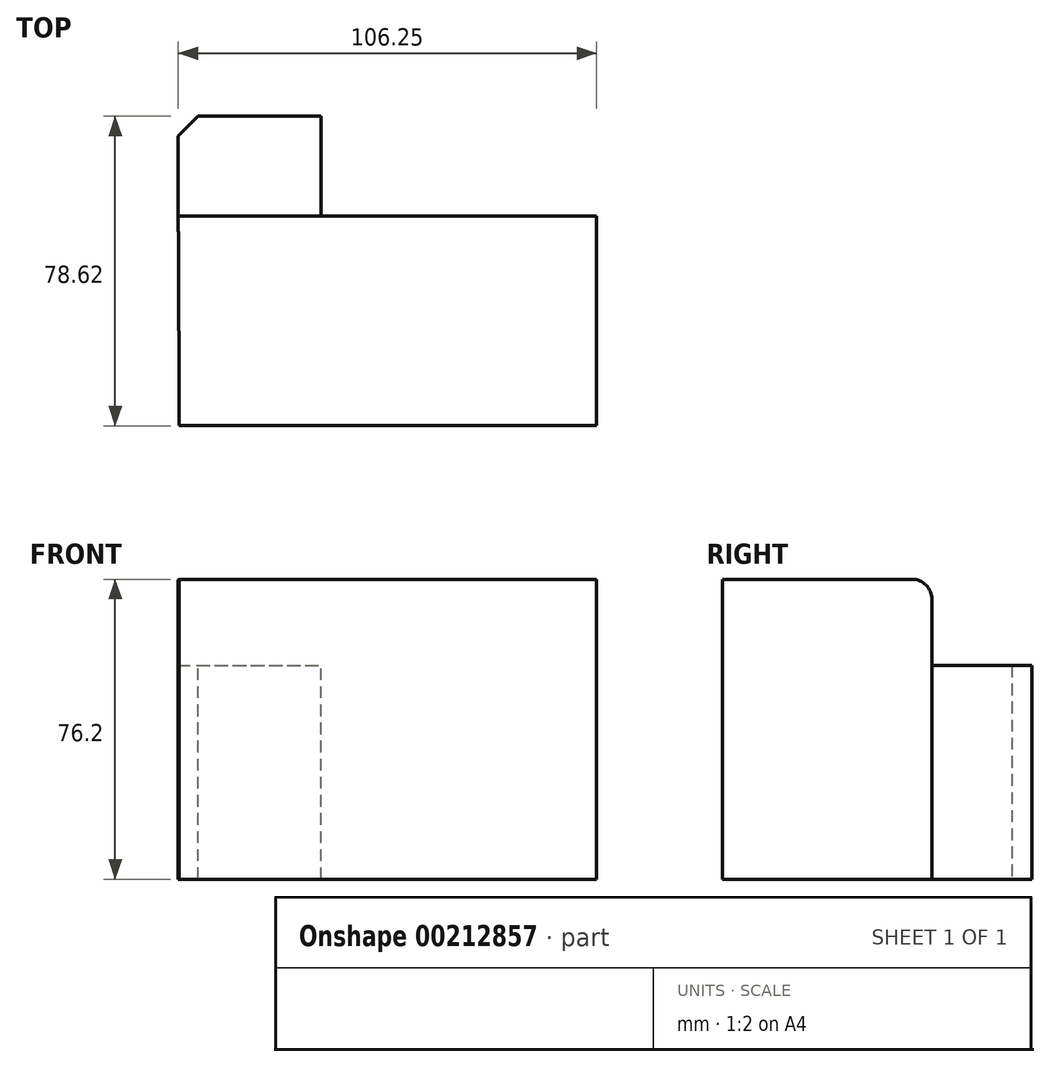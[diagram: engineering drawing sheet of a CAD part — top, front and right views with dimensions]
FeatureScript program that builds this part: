
annotation { "Feature Type Name" : "Feature", "Feature Type Description" : "" }
export const myFeature = defineFeature(function(context is Context, id is Id, definition is map)
    precondition{}
    {
        {
            var Q0;
            Q0=qCreatedBy(makeId("Top.planeOp"),FACE);
            var sketch = newSketch(context, id + "F0", { "sketchPlane" : qUnion([Q0])});
            skLineSegment(sketch, "E0", {"start": v(-76.37, 7.19) * mm, "end": v(29.88, 7.19) * mm});
            skLineSegment(sketch, "E1", {"start": v(29.88, 7.19) * mm, "end": v(29.88, -46.03) * mm});
            skLineSegment(sketch, "E2", {"start": v(29.88, -46.03) * mm, "end": v(-76.18, -46.03) * mm});
            skLineSegment(sketch, "E3", {"start": v(-76.37, 7.19) * mm, "end": v(-76.18, -46.03) * mm});
            skSolve(sketch);
        }
        {
            var Q0;
            Q0 = qSketchRegion(id + "F0", true);
            extrude(context, id + "F1", {"entities" : qUnion([Q0]), "depth" : 76.2 * mm});
        }
        {
            var Q0;
            Q0=makeQuery(id+"F1.opExtrude","SWEPT_FACE",FACE,{"disambiguationData":[OSD([sQuery(id+"F0.wireOp",EDGE,"E0")])]});
            var sketch = newSketch(context, id + "F2", { "sketchPlane" : qUnion([Q0])});
            skLineSegment(sketch, "E4.bottom", {"start": v(76.37, 0) * mm, "end": v(40.11, 0) * mm});
            skLineSegment(sketch, "E4.top", {"start": v(76.37, 54.3) * mm, "end": v(40.11, 54.3) * mm});
            skLineSegment(sketch, "E4.left", {"start": v(76.37, 0) * mm, "end": v(76.37, 54.3) * mm});
            skLineSegment(sketch, "E4.right", {"start": v(40.11, 0) * mm, "end": v(40.11, 54.3) * mm});
            skSolve(sketch);
        }
        {
            var Q0;
            Q0=makeQuery(id+"F2.imprint","IMPRINT",FACE,{"disambiguationData":[TD([[makeQuery(id+"F2.imprint","IMPRINT",EDGE,{"derivedFrom":sQuery(id+"F2.wireOp",EDGE,"E4.bottom")}),-1.0]])]});
            extrude(context, id + "F3", {"entities" : qUnion([Q0]), "operationType" : NewBodyOperationType.ADD, "depth" : 25.4 * mm});
        }
        {
            var Q0;
            Q0=makeQuery(id+"F3.opExtrude","CAP_EDGE",EDGE,{"disambiguationData":[OSD([sQuery(id+"F2.wireOp",EDGE,"E4.left")])],"isStart":false});
            chamfer(context, id + "F4", {"entities" : qUnion([Q0]), "width" : 5.08 * mm, "tangentPropagation" : true});
        }
        {
            var Q0;
            Q0=makeQuery(id+"F1.opExtrude","CAP_EDGE",EDGE,{"disambiguationData":[OSD([sQuery(id+"F0.wireOp",EDGE,"E0")])],"isStart":false});
            fillet(context, id + "F5", {"entities" : qUnion([Q0]), "radius" : 5.08 * mm, "tangentPropagation" : true, "allowEdgeOverflow" : false});
        }
    });
